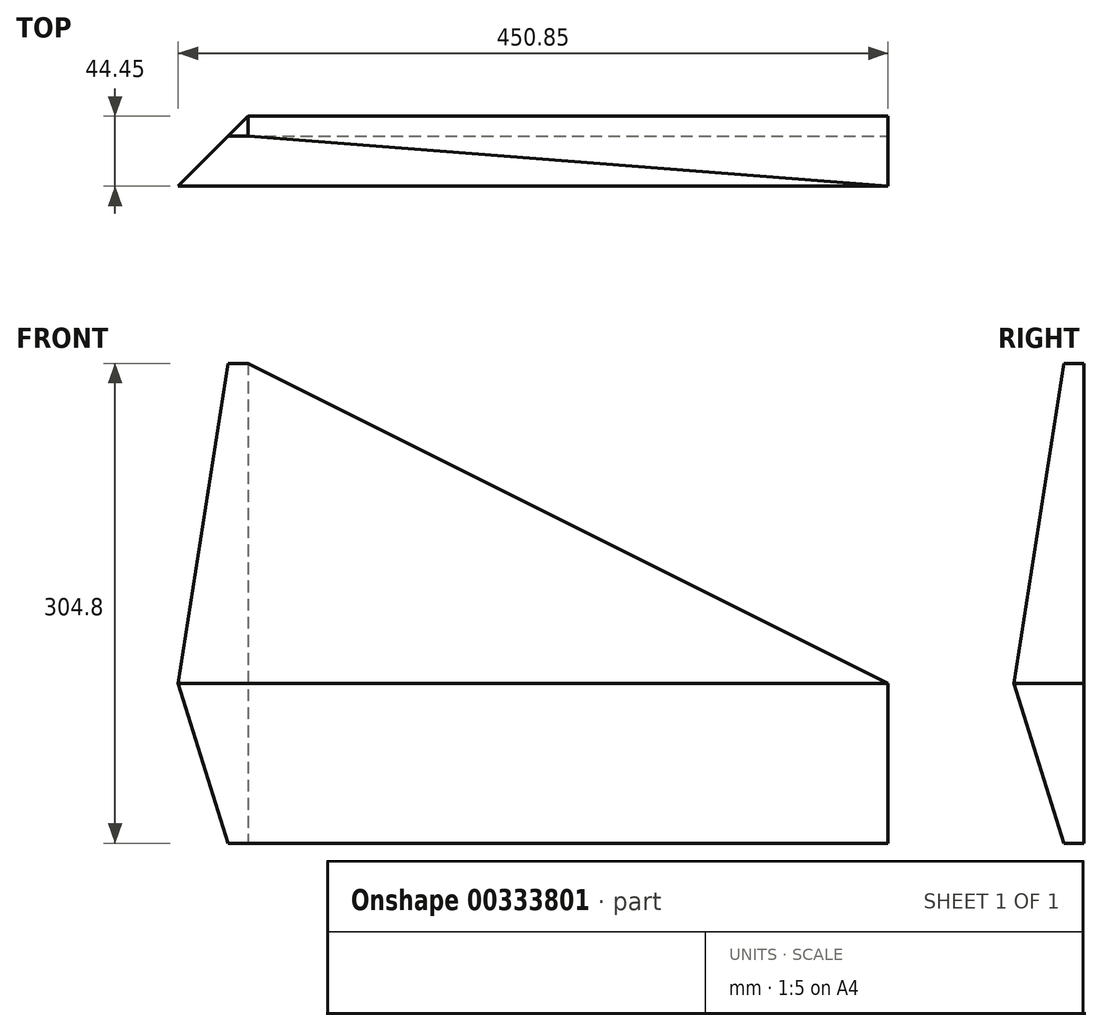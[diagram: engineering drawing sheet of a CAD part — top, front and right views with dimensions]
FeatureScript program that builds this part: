
annotation { "Feature Type Name" : "Feature", "Feature Type Description" : "" }
export const myFeature = defineFeature(function(context is Context, id is Id, definition is map)
    precondition{}
    {
        {
            var Q0;
            Q0=qCreatedBy(makeId("Front.planeOp"),FACE);
            var sketch = newSketch(context, id + "F0", { "sketchPlane" : qUnion([Q0])});
            skLineSegment(sketch, "E0.bottom", {"start": v(-74.09, 0) * mm, "end": v(383.11, 0) * mm});
            skLineSegment(sketch, "E0.top", {"start": v(-74.09, 304.8) * mm, "end": v(383.11, 304.8) * mm});
            skLineSegment(sketch, "E0.left", {"start": v(-74.09, 0) * mm, "end": v(-74.09, 304.8) * mm});
            skLineSegment(sketch, "E0.right", {"start": v(383.11, 0) * mm, "end": v(383.11, 304.8) * mm});
            skSolve(sketch);
        }
        {
            var Q0;
            Q0=qSketchRegion(id+"F0",true);
            extrude(context, id + "F1", {"entities" : qUnion([Q0]), "depth" : 44.45 * mm});
        }
        {
            var Q0;
            Q0=makeQuery(id+"F1.opExtrude","SWEPT_FACE",FACE,{"disambiguationData":[OSD([sQuery(id+"F0.wireOp",EDGE,"E0.right")])]});
            var sketch = newSketch(context, id + "F2", { "sketchPlane" : qUnion([Q0])});
            skLineSegment(sketch, "E1", {"start": v(-12.7, 304.8) * mm, "end": v(-44.45, 101.6) * mm});
            skLineSegment(sketch, "E2", {"start": v(-82.84, 0) * mm, "end": v(-82.84, 304.8) * mm});
            skPoint(sketch, "E2.endSnap0", {"position": v(-22.23, 304.8) * mm});
            skLineSegment(sketch, "E3", {"start": v(-82.84, 304.8) * mm, "end": v(-12.7, 304.8) * mm});
            skLineSegment(sketch, "E4", {"start": v(-44.45, 101.6) * mm, "end": v(-12.7, 0) * mm});
            skLineSegment(sketch, "E5", {"start": v(-12.7, 0) * mm, "end": v(-82.84, 0) * mm});
            skSolve(sketch);
        }
        {
            var Q0;
            Q0=qSketchRegion(id+"F2",true);
            extrude(context, id + "F3", {"entities" : qUnion([Q0]), "operationType" : NewBodyOperationType.REMOVE, "endBound" : BoundingType.THROUGH_ALL, "oppositeDirection" : true, "depth" : 25.4 * mm});
        }
        {
            var Q0;
            Q0=makeQuery(id+"F1.opExtrude","CAP_FACE",FACE,{"disambiguationData":[OSD([sQuery(id+"F0.wireOp",EDGE,"E0.bottom"),sQuery(id+"F0.wireOp",EDGE,"E0.top"),sQuery(id+"F0.wireOp",EDGE,"E0.left"),sQuery(id+"F0.wireOp",EDGE,"E0.right")])],"isStart":true});
            var sketch = newSketch(context, id + "F4", { "sketchPlane" : qUnion([Q0])});
            skLineSegment(sketch, "E6", {"start": v(23.29, 304.8) * mm, "end": v(-383.11, 101.6) * mm});
            skLineSegment(sketch, "E7", {"start": v(-383.11, 101.6) * mm, "end": v(-383.11, 304.8) * mm});
            skLineSegment(sketch, "E8", {"start": v(-383.11, 304.8) * mm, "end": v(23.29, 304.8) * mm});
            skSolve(sketch);
        }
        {
            var Q0;
            Q0 = qSketchRegion(id + "F4", true);
            extrude(context, id + "F5", {"entities" : qUnion([Q0]), "operationType" : NewBodyOperationType.REMOVE, "endBound" : BoundingType.THROUGH_ALL, "oppositeDirection" : true, "depth" : 25.4 * mm});
        }
        {
            var Q0;
            Q0=makeQuery(id+"F1.opExtrude","SWEPT_FACE",FACE,{"disambiguationData":[OSD([sQuery(id+"F0.wireOp",EDGE,"E0.bottom")])]});
            var sketch = newSketch(context, id + "F6", { "sketchPlane" : qUnion([Q0])});
            skLineSegment(sketch, "E9", {"start": v(-74.09, 0) * mm, "end": v(-23.29, 0) * mm});
            skLineSegment(sketch, "E10", {"start": v(-23.29, 0) * mm, "end": v(-74.09, 50.8) * mm});
            skPoint(sketch, "E10.endSnap0", {"position": v(-74.09, 6.35) * mm});
            skLineSegment(sketch, "E11", {"start": v(-74.09, 50.8) * mm, "end": v(-74.09, 0) * mm});
            skSolve(sketch);
        }
        {
            var Q0;
            Q0 = qSketchRegion(id + "F6", true);
            extrude(context, id + "F7", {"entities" : qUnion([Q0]), "operationType" : NewBodyOperationType.REMOVE, "endBound" : BoundingType.THROUGH_ALL, "oppositeDirection" : true, "depth" : 25.4 * mm});
        }
    });
